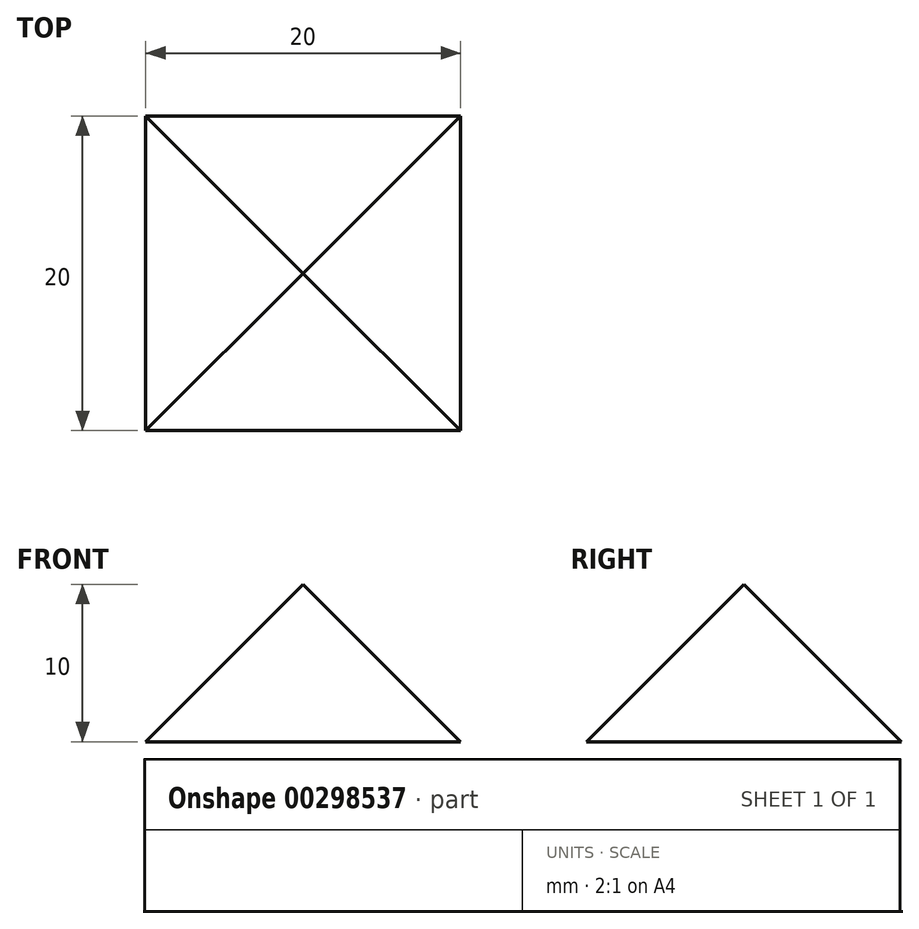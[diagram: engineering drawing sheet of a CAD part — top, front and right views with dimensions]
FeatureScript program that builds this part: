
annotation { "Feature Type Name" : "Feature", "Feature Type Description" : "" }
export const myFeature = defineFeature(function(context is Context, id is Id, definition is map)
    precondition{}
    {
        {
            var Q0;
            Q0=qCreatedBy(makeId("Front.planeOp"),FACE);
            var sketch = newSketch(context, id + "F0", { "sketchPlane" : qUnion([Q0])});
            skLineSegment(sketch, "E0", {"start": v(0, 0) * mm, "end": v(10, 0) * mm});
            skLineSegment(sketch, "E1", {"start": v(10, 0) * mm, "end": v(0, 10) * mm});
            skLineSegment(sketch, "E2", {"start": v(0, 10) * mm, "end": v(0, 0) * mm});
            skSolve(sketch);
        }
        {
            var Q0;
            Q0=qCreatedBy(makeId("Top.planeOp"),FACE);
            var sketch = newSketch(context, id + "F1", { "sketchPlane" : qUnion([Q0])});
            skLineSegment(sketch, "E3.bottom", {"start": v(-10, 10) * mm, "end": v(10, 10) * mm});
            skLineSegment(sketch, "E3.top", {"start": v(-10, -10) * mm, "end": v(10, -10) * mm});
            skLineSegment(sketch, "E3.left", {"start": v(-10, 10) * mm, "end": v(-10, -10) * mm});
            skLineSegment(sketch, "E3.right", {"start": v(10, 10) * mm, "end": v(10, -10) * mm});
            skPoint(sketch, "E3.middle", {"position": v(0, 0) * mm});
            skSolve(sketch);
        }
        {
            var Q0;
            Q0 = qSketchRegion(id + "F0", true);
            var Q1;
            Q1=sQuery(id+"F1.wireOp",EDGE,"E3.top");
            var Q2;
            Q2=sQuery(id+"F1.wireOp",EDGE,"E3.right");
            var Q3;
            Q3=sQuery(id+"F1.wireOp",EDGE,"E3.bottom");
            var Q4;
            Q4=sQuery(id+"F1.wireOp",EDGE,"E3.left");
            sweep(context, id + "F2", {"profiles" : qUnion([Q0]), "path" : qUnion([Q1, Q2, Q3, Q4])});
        }
    });
